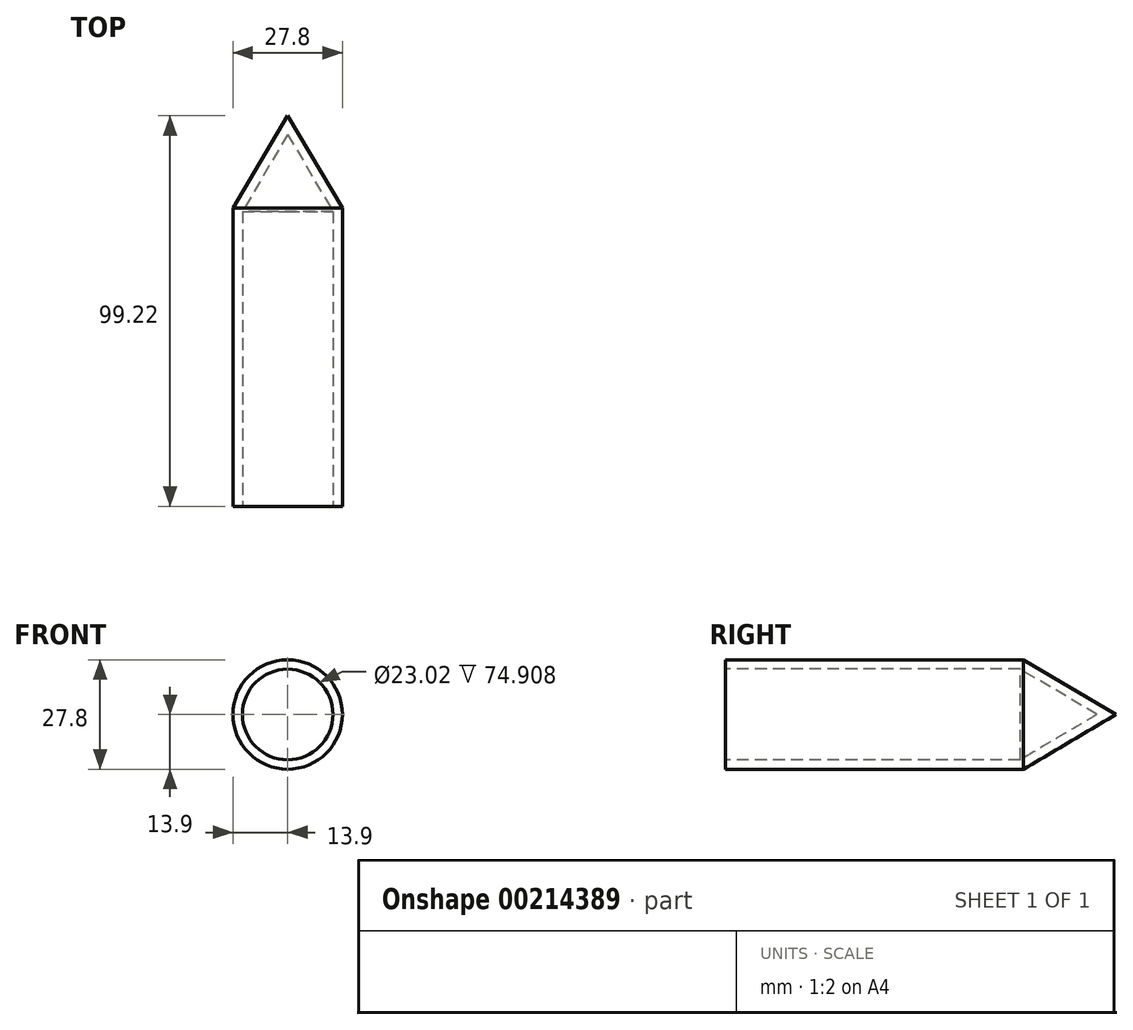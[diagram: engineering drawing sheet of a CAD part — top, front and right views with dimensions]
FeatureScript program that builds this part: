
annotation { "Feature Type Name" : "Feature", "Feature Type Description" : "" }
export const myFeature = defineFeature(function(context is Context, id is Id, definition is map)
    precondition{}
    {
        {
            var Q0;
            Q0=qCreatedBy(makeId("Top.planeOp"),FACE);
            var sketch = newSketch(context, id + "F0", { "sketchPlane" : qUnion([Q0])});
            skLineSegment(sketch, "E0", {"start": v(0, 71.54) * mm, "end": v(-13.9, 48.1) * mm});
            skLineSegment(sketch, "E1", {"start": v(-13.9, 48.1) * mm, "end": v(-13.9, -27.68) * mm});
            skLineSegment(sketch, "E2", {"start": v(-13.9, -27.68) * mm, "end": v(-11.5, -27.68) * mm});
            skLineSegment(sketch, "E3", {"start": v(-11.5, -27.68) * mm, "end": v(-11.5, 47.22) * mm});
            skLineSegment(sketch, "E4", {"start": v(-11.5, 47.22) * mm, "end": v(0, 66.77) * mm});
            skLineSegment(sketch, "E5", {"start": v(0, 66.77) * mm, "end": v(0, 71.54) * mm});
            skSolve(sketch);
        }
        {
            var Q0;
            Q0=makeQuery(id+"F0.imprint","IMPRINT",FACE,{"disambiguationData":[TD([[makeQuery(id+"F0.imprint","IMPRINT",EDGE,{"derivedFrom":sQuery(id+"F0.wireOp",EDGE,"E0")}),1.0]])]});
            var Q1;
            Q1=sQuery(id+"F0.wireOp",EDGE,"E5");
            revolve(context, id + "F1", {"entities" : qUnion([Q0]), "axis" : qUnion([Q1]), "revolveType" : RevolveType.FULL});
        }
    });
